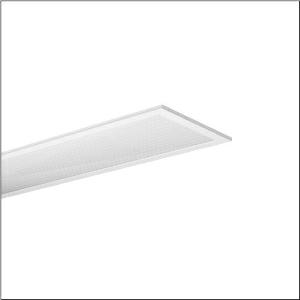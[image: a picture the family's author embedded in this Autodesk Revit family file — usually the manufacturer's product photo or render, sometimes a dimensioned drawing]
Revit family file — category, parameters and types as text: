
# Revit family: apollon_r__21_linear_51mq14w72412_c4b7
name_source: partatom
category: Lighting Fixtures
units: mm (PartAtom-declared; Revit-internal decimal feet)

## family parameters
Cut with Voids When Loaded = No
Host = Face
Light Source = No
Part Type = Normal
Room Calculation Point = No
Round Connector Dimension = Use Diameter
Shared = No

## types (1)
- Apollon® 21 linear (1 x LED, 4000 lm, 33 W, 4000K)
    Apparent Load = 33 VA
    CIE Flux Codes = 60 89 97 100 100
    Color Rendering = 80
    Color Temperature = 4000K
    Default Elevation = 1800 mm
    Description = Apollon® 21 linear, office luminaire, primary optical cover: micro prismatic cover, CAT 2 (L<= 3000cd/m²), light emission: direct distribution, primary light characteristic: symmetric, installation type: lay-in mounting, LED, rated luminous flux: 4.000lm, luminous efficacy: 121lm/W, light colour: 840, colour temperature: 4000K, with terminal, 3-pole, mains connection: 220..240V, AC, 50/60Hz, rated input power: 33W, housing, of aluminium, coated, pure white, length: 1.245mm, width: 307mm, height: 30mm, housing upper side, of sheet steel, galvanised, protection rating (complete): IP20, protection rating (lamp compartment, on room side): IP50, insulation class (complete): insulation class II (safety insulation), certification: CE, ENEC, impact resistance: IK03, permissible operating ambient temperature: -20..+45°C, permissible storage temperature: -40..+80°C, packaging unit: 1 piece
    Height = 0 mm  [stored 0 ft]
    Lamp = 1 x LED
    Lamp Light Flux = 4000 lm
    Lamp Power = 33 W
    Lamp count = 1
    Length = 1245 mm
    Luminous efficacy = 121 lm/W
    Manufacturer = Siteco
    ModVariant = No
    Model = 51MQ14W72412
    Mounting Place = Ceiling
    Mounting Type = Recessed
    Number of Poles = 1
    OnlyDefault = Yes
    Power Factor = 1
    Product Name = Apollon® 21 linear
    Product group = office luminaire | ceiling recessed
    ProductGroupID = 401
    Protection Class = Protection class II
    Protection Degree = IP 20
    RLX_Detail_Level = 1
    RLX_Emergency_Light_Flux = 0 lm
    RLX_Emergency_Type = 0
    RLX_Emergency_Type_DB = No
    RlxData = <blob elided: 17325 chars, md5=5b5d4756>
    Socket = socket
    Standby Power = 0 W
    System Light Flux = 4000 lm
    System Power = 33 W
    Type Comments = Product without accessories
    Type Image = l_1291045.jpg
    URL = http://relux.com
    VarID = ---
    Voltage = 0 V
    Weight = 0.00 kg
    Width = 307 mm

note: [stored X ft] marks values corroborated as IEEE doubles in the binary element streams (Revit-internal decimal feet)

## geometry (parser evidence)
native form markers: Blend x4, Sweep x11
no freeform markers — native parametric forms only
